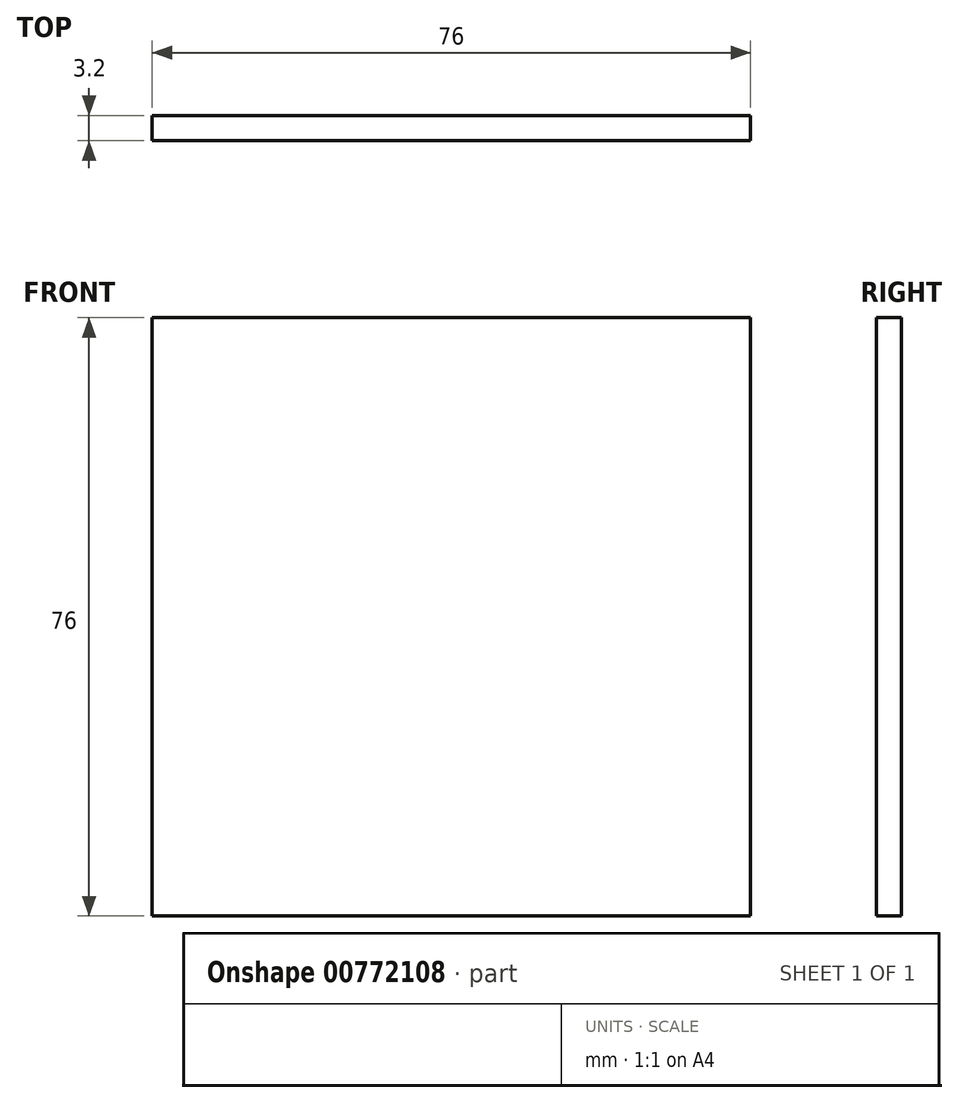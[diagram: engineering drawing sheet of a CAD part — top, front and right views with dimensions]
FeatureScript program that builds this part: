
annotation { "Feature Type Name" : "Feature", "Feature Type Description" : "" }
export const myFeature = defineFeature(function(context is Context, id is Id, definition is map)
    precondition{}
    {
        {
            var Q0;
            Q0=qCreatedBy(makeId("Front.planeOp"),FACE);
            var sketch = newSketch(context, id + "F0", { "sketchPlane" : qUnion([Q0])});
            skLineSegment(sketch, "E0.bottom", {"start": v(38, 38) * mm, "end": v(-38, 38) * mm});
            skLineSegment(sketch, "E0.top", {"start": v(38, -38) * mm, "end": v(-38, -38) * mm});
            skLineSegment(sketch, "E0.left", {"start": v(38, 38) * mm, "end": v(38, -38) * mm});
            skLineSegment(sketch, "E0.right", {"start": v(-38, 38) * mm, "end": v(-38, -38) * mm});
            skPoint(sketch, "E0.middle", {"position": v(0, 0) * mm});
            skSolve(sketch);
        }
        {
            var Q0;
            Q0 = qSketchRegion(id + "F0", true);
            extrude(context, id + "F1", {"entities" : qUnion([Q0]), "depth" : 3.2 * mm, "offsetDistance" : 25 * mm});
        }
    });
